# Revit family: Microphone-Tabletop-Q-SYS-NM-T1
name_source: partatom
category: Communication Devices
units: mm (PartAtom-declared; Revit-internal decimal feet)

## family parameters
Cut with Voids When Loaded = No
Host = Face
Maintain Annotation Orientation = No
OmniClass Number = 23.85.10.11.14.14.11
OmniClass Title = Microphones
Part Type = Normal
Room Calculation Point = No
Round Connector Dimension = Use Diameter
Shared = No

## types (3) — shared parameters
Body Material = Plastic - Q-SYS - Gray
Default Elevation = 48 "
Depth = 4.21 "
Description = Tabletop network PoE microphone.
Frequency Response = 100 Hz - 16 kHz, +/- 3 dB
Grille Material = Metal - Q-SYS - Mesh
Height = 1.1 "
Highlgiht Material 2 = Image - Q-SYS - Microphone 2
Highlight Material 1 = Image - Q-SYS - Microphone 1
IQ Category = Microphone
Latency = 0.0 s
Manufacturer = Q-SYS
Manufacturer URL = www.qsys.com
Model = NM-T1
Noise = 28
OmniClass Number = 23.85.10.11.14.14.11
Polar Pattern = Superdirective
Product Documentation Link = https://www.qsys.com
Product Page URL = https://www.qsys.com
URL = https://www.qsys.com
Weight = 1.50 lbm
Width = 4.21 "
zero-valued in all types: Cost MSRP, Cost Project, Heat Load Active, Heat Load Standby

## per-type parameters (varying)
| type | LED Material | Weight Dimensional | Weight Product |
| Green | Plastic - Q-SYS - LED Green | 1.5 | 1.5 |
| Blue | Plastic - Q-SYS - LED Blue | 0 | 0 |
| Red | Plastic - Q-SYS - LED Red | 0 | 0 |

note: column(s) folded — value = type name in every type: Type Comments

## geometry (parser evidence)
native form markers: Sweep x3
no freeform markers — native parametric forms only
